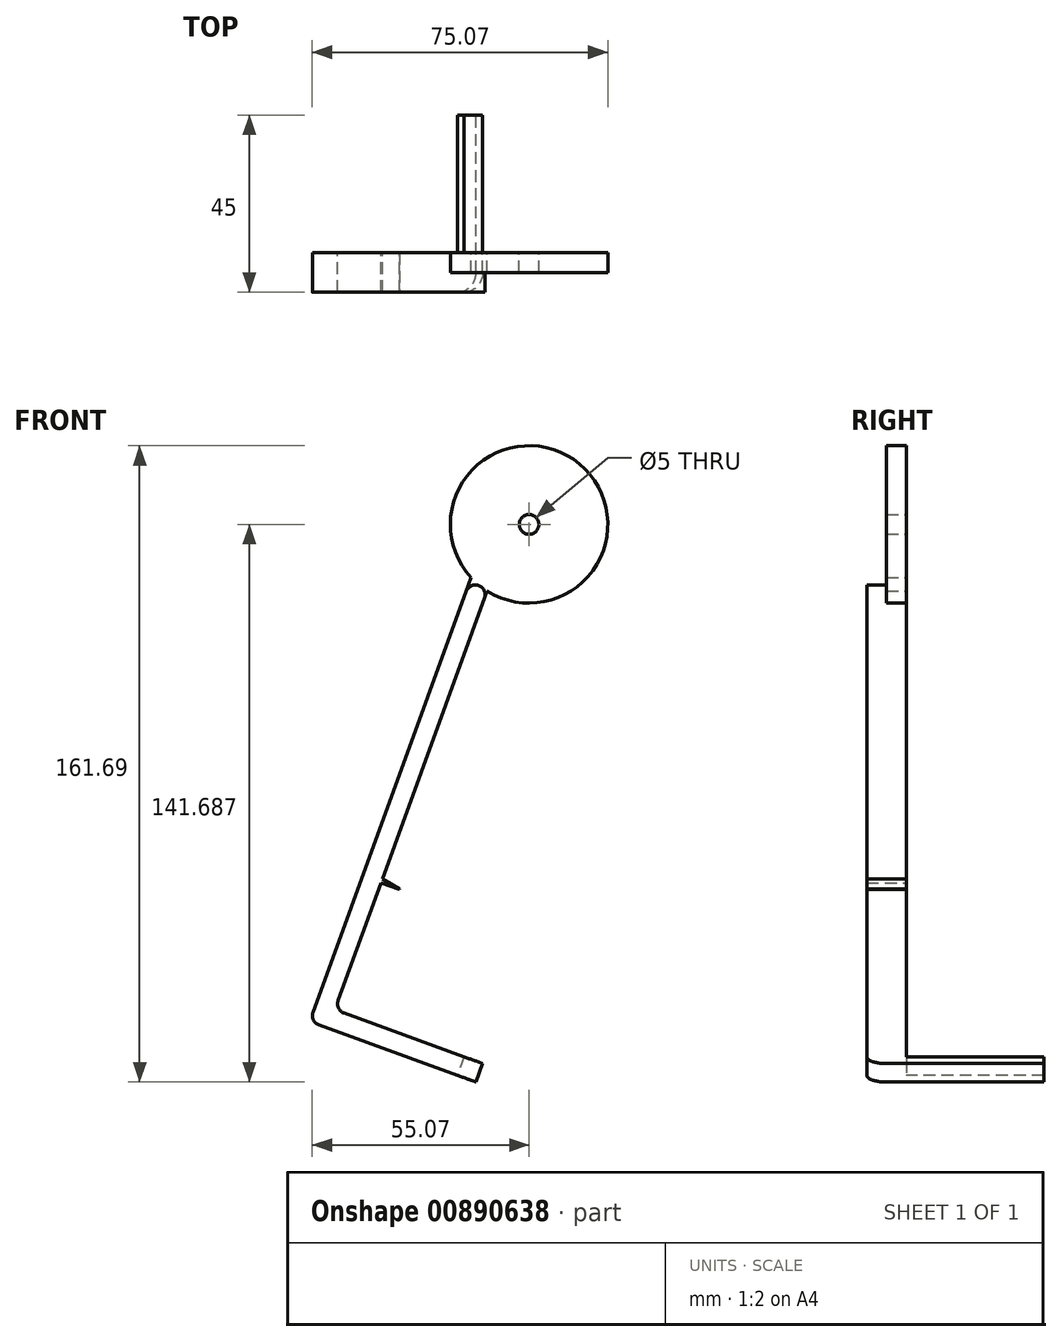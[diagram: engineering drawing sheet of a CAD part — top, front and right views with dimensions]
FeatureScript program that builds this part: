
annotation { "Feature Type Name" : "Feature", "Feature Type Description" : "" }
export const myFeature = defineFeature(function(context is Context, id is Id, definition is map)
    precondition{}
    {
        {
            var Q0;
            Q0=qCreatedBy(makeId("Front.planeOp"),FACE);
            var sketch = newSketch(context, id + "F0", { "sketchPlane" : qUnion([Q0])});
            skCircle(sketch, "E0", {"center": v(0, 33.82) * mm, "radius": 2.5 * mm});
            skLineSegment(sketch, "E1", {"start": v(0, 70.54) * mm, "end": v(0, -41.15) * mm, "construction": true});
            skLineSegment(sketch, "E2", {"start": v(-37.62, -57.23) * mm, "end": v(-42.32, -55.52) * mm});
            skLineSegment(sketch, "E3", {"start": v(-37.62, -57.23) * mm, "end": v(-32.92, -58.94) * mm});
            skLineSegment(sketch, "E4", {"start": v(-32.92, -58.94) * mm, "end": v(-32.58, -58) * mm});
            skLineSegment(sketch, "E5", {"start": v(-32.58, -58) * mm, "end": v(-37.28, -56.3) * mm});
            skCircle(sketch, "E6", {"center": v(0, 33.82) * mm, "radius": 20 * mm});
            skLineSegment(sketch, "E7", {"start": v(-10.65, 16.89) * mm, "end": v(-37.28, -56.3) * mm});
            skLineSegment(sketch, "E8", {"start": v(-14.73, 20.29) * mm, "end": v(-42.32, -55.52) * mm});
            skLineSegment(sketch, "E9", {"start": v(-14.73, 20.29) * mm, "end": v(-55.77, -92.48) * mm});
            skLineSegment(sketch, "E10", {"start": v(-10.65, 16.89) * mm, "end": v(-51.07, -94.19) * mm});
            skLineSegment(sketch, "E11", {"start": v(-55.77, -92.48) * mm, "end": v(-51.07, -94.19) * mm});
            skLineSegment(sketch, "E12", {"start": v(-51.07, -94.19) * mm, "end": v(-13.49, -107.87) * mm});
            skLineSegment(sketch, "E13", {"start": v(-13.49, -107.87) * mm, "end": v(-11.78, -103.17) * mm});
            skLineSegment(sketch, "E14", {"start": v(-11.78, -103.17) * mm, "end": v(-49.36, -89.49) * mm});
            skLineSegment(sketch, "E15", {"start": v(-16.47, -101.46) * mm, "end": v(-18.18, -106.16) * mm});
            skSolve(sketch);
        }
        {
            var Q0;
            Q0=makeQuery(id+"F0.imprint","IMPRINT",FACE,{"disambiguationData":[TD([[makeQuery(id+"F0.imprint","IMPRINT",EDGE,{"derivedFrom":sQuery(id+"F0.wireOp",EDGE,"E0")}),-1.0]])]});
            var Q1;
            {var subQ5=sQuery(id+"F0.wireOp",EDGE,"E2");Q1=makeQuery(id+"F0.imprint","IMPRINT",FACE,{"disambiguationData":[TD([[makeQuery(id+"F0.imprint","IMPRINT",EDGE,{"derivedFrom":subQ5}),-1.0]])]});}
            var Q2;
            {var subQ0=sQuery(id+"F0.wireOp",EDGE,"E3");Q2=makeQuery(id+"F0.imprint","IMPRINT",FACE,{"disambiguationData":[TD([[makeQuery(id+"F0.imprint","IMPRINT",EDGE,{"derivedFrom":subQ0}),1.0]])]});}
            var Q3;
            {var subQ3=sQuery(id+"F0.wireOp",EDGE,"E2");Q3=makeQuery(id+"F0.imprint","IMPRINT",FACE,{"disambiguationData":[TD([[makeQuery(id+"F0.imprint","IMPRINT",EDGE,{"derivedFrom":subQ3}),1.0]])]});}
            var Q4;
            {var subQ0=sQuery(id+"F0.wireOp",EDGE,"E12");Q4=makeQuery(id+"F0.imprint","IMPRINT",FACE,{"disambiguationData":[TD([[makeQuery(id+"F0.imprint","IMPRINT",EDGE,{"derivedFrom":subQ0}),1.0]])]});}
            extrude(context, id + "F1", {"entities" : qUnion([Q0, Q1, Q2, Q3, Q4]), "depth" : 5 * mm, "offsetDistance" : 25 * mm});
        }
        {
            var Q0;
            {var subQ5=sQuery(id+"F0.wireOp",EDGE,"E2");Q0=makeQuery(id+"F0.imprint","IMPRINT",FACE,{"disambiguationData":[TD([[makeQuery(id+"F0.imprint","IMPRINT",EDGE,{"derivedFrom":subQ5}),-1.0]])]});}
            var Q1;
            {var subQ3=sQuery(id+"F0.wireOp",EDGE,"E2");Q1=makeQuery(id+"F0.imprint","IMPRINT",FACE,{"disambiguationData":[TD([[makeQuery(id+"F0.imprint","IMPRINT",EDGE,{"derivedFrom":subQ3}),1.0]])]});}
            var Q2;
            {var subQ0=sQuery(id+"F0.wireOp",EDGE,"E12");Q2=makeQuery(id+"F0.imprint","IMPRINT",FACE,{"disambiguationData":[TD([[makeQuery(id+"F0.imprint","IMPRINT",EDGE,{"derivedFrom":subQ0}),1.0]])]});}
            var Q3;
            {var subQ0=sQuery(id+"F0.wireOp",EDGE,"E3");Q3=makeQuery(id+"F0.imprint","IMPRINT",FACE,{"disambiguationData":[TD([[makeQuery(id+"F0.imprint","IMPRINT",EDGE,{"derivedFrom":subQ0}),1.0]])]});}
            extrude(context, id + "F2", {"entities" : qUnion([Q0, Q1, Q2, Q3]), "operationType" : NewBodyOperationType.ADD, "depth" : 10 * mm, "offsetDistance" : 25 * mm});
        }
        {
            var Q0;
            Q0=makeQuery(id+"F2.opExtrude","SWEPT_EDGE",EDGE,{"disambiguationData":[OSD([sQuery(id+"F0.wireOp",EDGE,"E6"),sQuery(id+"F0.wireOp",EDGE,"E10")])]});
            var Q1;
            Q1=makeQuery(id+"F2.opExtrude","SWEPT_EDGE",EDGE,{"disambiguationData":[OSD([sQuery(id+"F0.wireOp",EDGE,"E6"),sQuery(id+"F0.wireOp",EDGE,"E9")])]});
            fillet(context, id + "F3", {"entities" : qUnion([Q0, Q1]), "radius" : 2.5 * mm, "tangentPropagation" : true, "allowEdgeOverflow" : false});
        }
        {
            var Q0;
            {var subQ0=sQuery(id+"F0.wireOp",EDGE,"E11");var subQ1=sQuery(id+"F0.wireOp",EDGE,"E9");Q0=makeQuery(id+"F2.boolean.opBoolean","MERGE",EDGE,{"derivedFrom":[makeQuery(id+"F1.opExtrude","SWEPT_EDGE",EDGE,{"disambiguationData":[OSD([subQ1,subQ0])]}),makeQuery(id+"F2.opExtrude","SWEPT_EDGE",EDGE,{"disambiguationData":[OSD([subQ1,subQ0])]})]});}
            var Q1;
            Q1=makeQuery(id+"F2.opExtrude","CAP_EDGE",EDGE,{"disambiguationData":[OSD([sQuery(id+"F0.wireOp",EDGE,"E13")])],"isStart":false});
            fillet(context, id + "F4", {"entities" : qUnion([Q0, Q1]), "radius" : 5 * mm, "tangentPropagation" : true, "allowEdgeOverflow" : false});
        }
        {
            var Q0;
            {var subQ0=sQuery(id+"F0.wireOp",EDGE,"E5");var subQ1=sQuery(id+"F0.wireOp",EDGE,"E4");Q0=makeQuery(id+"F2.boolean.opBoolean","MERGE",EDGE,{"derivedFrom":[makeQuery(id+"F1.opExtrude","SWEPT_EDGE",EDGE,{"disambiguationData":[OSD([subQ1,subQ0])]}),makeQuery(id+"F2.opExtrude","SWEPT_EDGE",EDGE,{"disambiguationData":[OSD([subQ1,subQ0])]})]});}
            chamfer(context, id + "F5", {"entities" : qUnion([Q0]), "chamferType" : ChamferType.OFFSET_ANGLE, "width" : 5 * mm, "oppositeDirection" : false, "angle" : 10 * degree, "tangentPropagation" : true});
        }
        {
            var Q0;
            {var subQ0=sQuery(id+"F0.wireOp",EDGE,"E13");Q0=makeQuery(id+"F0.imprint","IMPRINT",FACE,{"disambiguationData":[TD([[makeQuery(id+"F0.imprint","IMPRINT",EDGE,{"derivedFrom":subQ0}),1.0]])]});}
            extrude(context, id + "F6", {"entities" : qUnion([Q0]), "operationType" : NewBodyOperationType.ADD, "oppositeDirection" : true, "depth" : 35 * mm, "offsetDistance" : 25 * mm});
        }
    });
